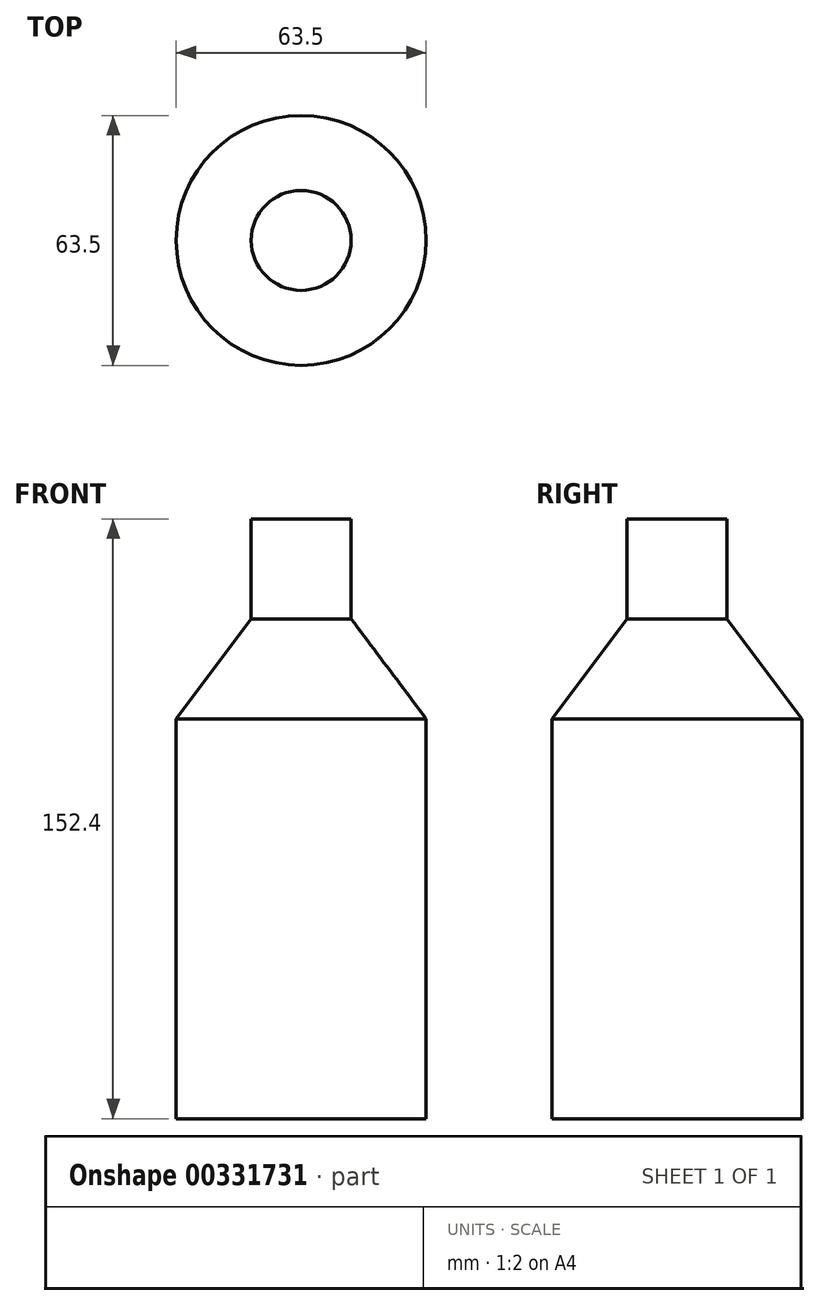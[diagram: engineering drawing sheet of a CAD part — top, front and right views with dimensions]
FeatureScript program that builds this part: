
annotation { "Feature Type Name" : "Feature", "Feature Type Description" : "" }
export const myFeature = defineFeature(function(context is Context, id is Id, definition is map)
    precondition{}
    {
        {
            var Q0;
            Q0=qCreatedBy(makeId("Top.planeOp"),FACE);
            var sketch = newSketch(context, id + "F0", { "sketchPlane" : qUnion([Q0])});
            skCircle(sketch, "E0", {"center": v(0, 0) * mm, "radius": 31.75 * mm});
            skSolve(sketch);
        }
        {
            var Q0;
            Q0=qCreatedBy(makeId("Top.planeOp"),FACE);
            cPlane(context, id + "F1", {"entities" : qUnion([Q0]), "cplaneType" : CPlaneType.OFFSET, "offset" : 101.6 * mm, "width" : 152.4 * mm, "height" : 152.4 * mm});
        }
        {
            var Q0;
            Q0=qCreatedBy(id+"F1.planeOp",FACE);
            var sketch = newSketch(context, id + "F2", { "sketchPlane" : qUnion([Q0])});
            skCircle(sketch, "E1", {"center": v(0, 0) * mm, "radius": 31.75 * mm});
            skSolve(sketch);
        }
        {
            var Q0;
            Q0=qCreatedBy(id+"F1.planeOp",FACE);
            cPlane(context, id + "F3", {"entities" : qUnion([Q0]), "cplaneType" : CPlaneType.OFFSET, "offset" : 25.4 * mm, "width" : 152.4 * mm, "height" : 152.4 * mm});
        }
        {
            var Q0;
            Q0=qCreatedBy(id+"F3.planeOp",FACE);
            var sketch = newSketch(context, id + "F4", { "sketchPlane" : qUnion([Q0])});
            skCircle(sketch, "E2", {"center": v(0, 0) * mm, "radius": 12.7 * mm});
            skSolve(sketch);
        }
        {
            var Q0;
            Q0=qCreatedBy(id+"F3.planeOp",FACE);
            cPlane(context, id + "F5", {"entities" : qUnion([Q0]), "cplaneType" : CPlaneType.OFFSET, "offset" : 25.4 * mm, "width" : 152.4 * mm, "height" : 152.4 * mm});
        }
        {
            var Q0;
            Q0=qCreatedBy(id+"F5.planeOp",FACE);
            var sketch = newSketch(context, id + "F6", { "sketchPlane" : qUnion([Q0])});
            skCircle(sketch, "E3", {"center": v(0, 0) * mm, "radius": 12.7 * mm});
            skSolve(sketch);
        }
        {
            var Q0;
            Q0 = qSketchRegion(id + "F4", true);
            var Q1;
            Q1 = qSketchRegion(id + "F6", true);
            loft(context, id + "F7", {"sheetProfilesArray" : [{ "sheetProfileEntities" : qUnion([Q0]) }, { "sheetProfileEntities" : qUnion([Q1]) }]});
        }
        {
            var Q0;
            Q0 = qSketchRegion(id + "F0", true);
            var Q1;
            Q1 = qSketchRegion(id + "F2", true);
            loft(context, id + "F8", {"sheetProfilesArray" : [{ "sheetProfileEntities" : qUnion([Q0]) }, { "sheetProfileEntities" : qUnion([Q1]) }]});
        }
        {
            var Q0;
            Q0 = qSketchRegion(id + "F2", true);
            var Q1;
            Q1 = qSketchRegion(id + "F4", true);
            loft(context, id + "F9", {"sheetProfilesArray" : [{ "sheetProfileEntities" : qUnion([Q0]) }, { "sheetProfileEntities" : qUnion([Q1]) }]});
        }
    });
